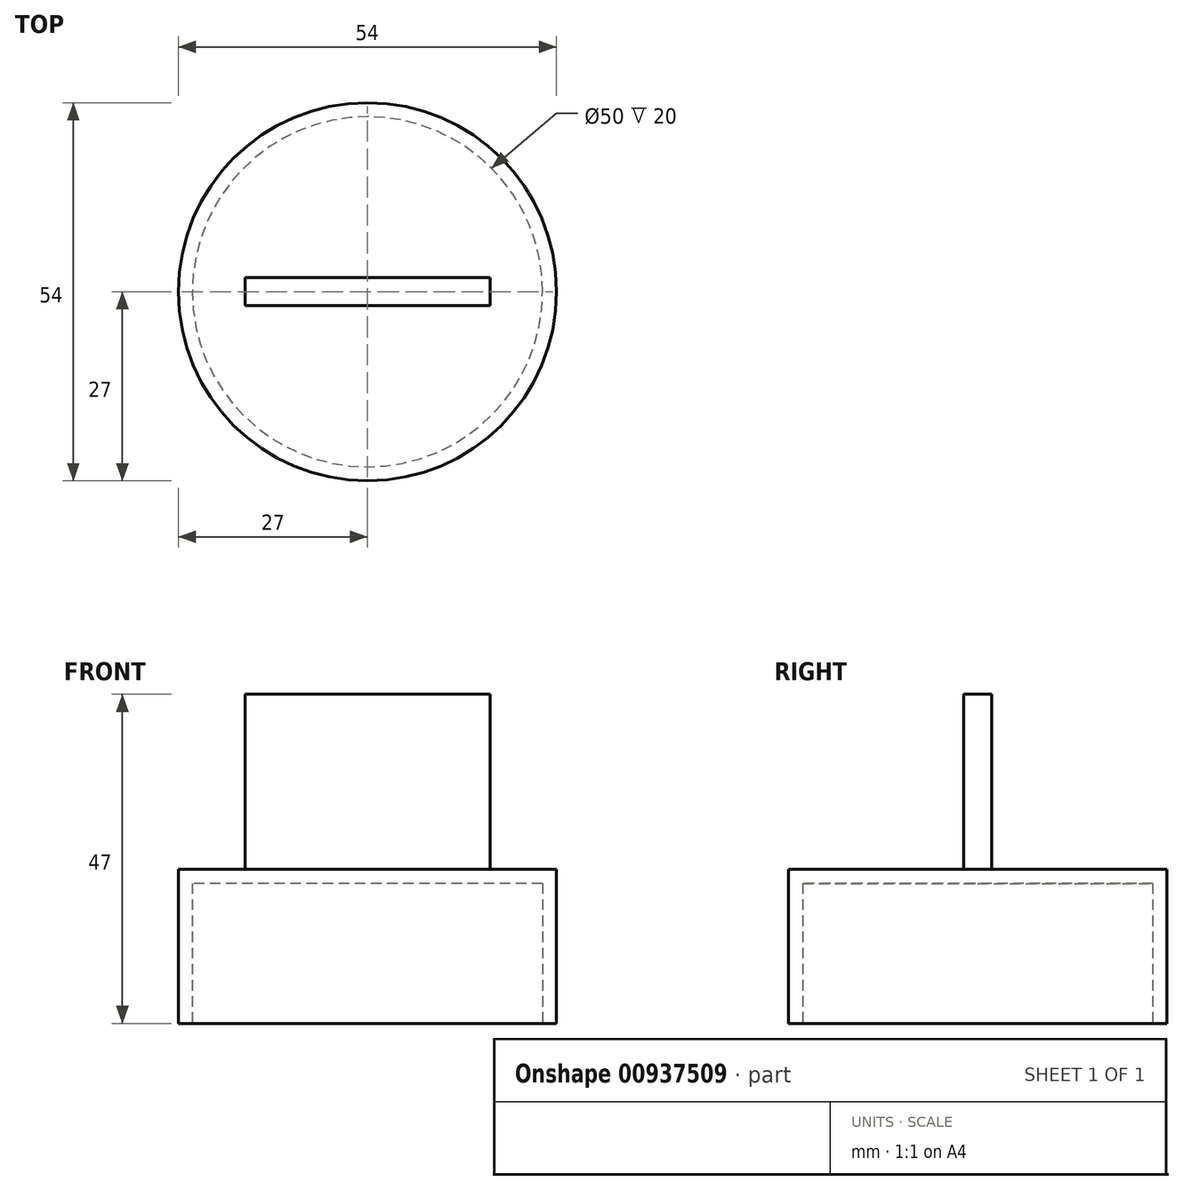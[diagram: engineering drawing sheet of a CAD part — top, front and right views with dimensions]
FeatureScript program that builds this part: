
annotation { "Feature Type Name" : "Feature", "Feature Type Description" : "" }
export const myFeature = defineFeature(function(context is Context, id is Id, definition is map)
    precondition{}
    {
        {
            var Q0;
            Q0=qCreatedBy(makeId("Top.planeOp"),FACE);
            var sketch = newSketch(context, id + "F0", { "sketchPlane" : qUnion([Q0])});
            skCircle(sketch, "E0", {"center": v(0, 0) * mm, "radius": 25 * mm});
            skCircle(sketch, "E1.0", {"center": v(0, 0) * mm, "radius": 27 * mm});
            skSolve(sketch);
        }
        {
            var Q0;
            Q0=makeQuery(id+"F0.imprint","IMPRINT",FACE,{"disambiguationData":[TD([[makeQuery(id+"F0.imprint","IMPRINT",EDGE,{"derivedFrom":sQuery(id+"F0.wireOp",EDGE,"E0")}),-1.0]])]});
            extrude(context, id + "F1", {"entities" : qUnion([Q0]), "depth" : 20 * mm, "offsetDistance" : 25 * mm});
        }
        {
            var Q0;
            Q0=makeQuery(id+"F1.opExtrude","CAP_FACE",FACE,{"disambiguationData":[OSD([sQuery(id+"F0.wireOp",EDGE,"E0"),sQuery(id+"F0.wireOp",EDGE,"E1.0")])],"isStart":false});
            var sketch = newSketch(context, id + "F2", { "sketchPlane" : qUnion([Q0])});
            skCircle(sketch, "E2.0", {"center": v(0, 0) * mm, "radius": 27 * mm});
            skSolve(sketch);
        }
        {
            var Q0;
            Q0 = qSketchRegion(id + "F2", true);
            extrude(context, id + "F3", {"entities" : qUnion([Q0]), "operationType" : NewBodyOperationType.ADD, "depth" : 2 * mm, "offsetDistance" : 25 * mm});
        }
        {
            var Q0;
            Q0=makeQuery(id+"F3.opExtrude","CAP_FACE",FACE,{"disambiguationData":[OSD([sQuery(id+"F2.wireOp",EDGE,"E2.0")])],"isStart":false});
            var sketch = newSketch(context, id + "F4", { "sketchPlane" : qUnion([Q0])});
            skLineSegment(sketch, "E3.bottom", {"start": v(17.5, 2) * mm, "end": v(-17.5, 2) * mm});
            skLineSegment(sketch, "E3.top", {"start": v(17.5, -2) * mm, "end": v(-17.5, -2) * mm});
            skLineSegment(sketch, "E3.left", {"start": v(17.5, 2) * mm, "end": v(17.5, -2) * mm});
            skLineSegment(sketch, "E3.right", {"start": v(-17.5, 2) * mm, "end": v(-17.5, -2) * mm});
            skPoint(sketch, "E3.middle", {"position": v(0, 0) * mm});
            skSolve(sketch);
        }
        {
            var Q0;
            Q0=makeQuery(id+"F4.imprint","IMPRINT",FACE,{"disambiguationData":[TD([[makeQuery(id+"F4.imprint","IMPRINT",EDGE,{"derivedFrom":sQuery(id+"F4.wireOp",EDGE,"E3.bottom")}),1.0]])]});
            extrude(context, id + "F5", {"entities" : qUnion([Q0]), "operationType" : NewBodyOperationType.ADD, "depth" : 25 * mm, "offsetDistance" : 25 * mm});
        }
    });
